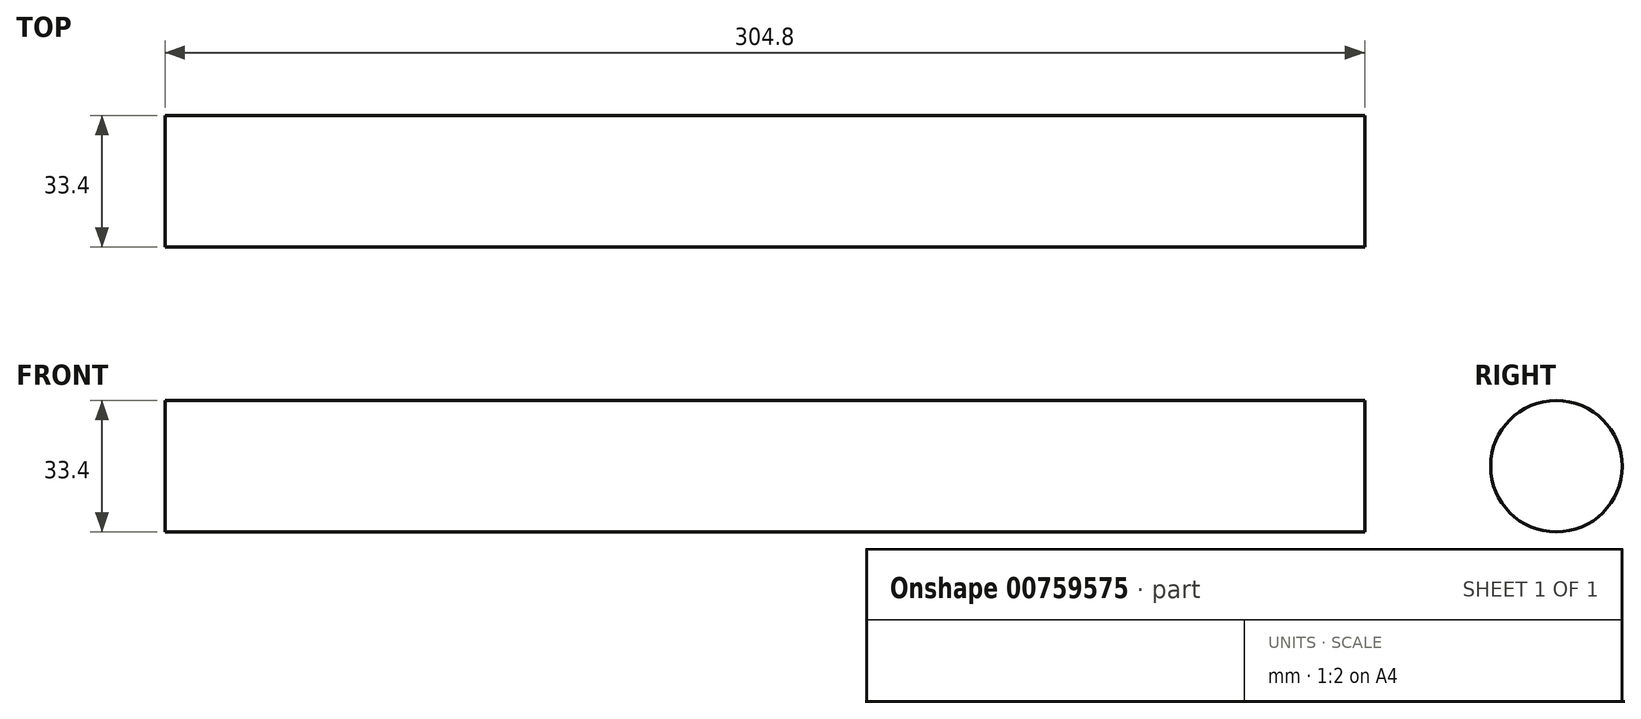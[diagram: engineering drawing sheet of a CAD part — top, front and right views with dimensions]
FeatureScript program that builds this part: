
annotation { "Feature Type Name" : "Feature", "Feature Type Description" : "" }
export const myFeature = defineFeature(function(context is Context, id is Id, definition is map)
    precondition{}
    {
        {
            var Q0;
            Q0=qCreatedBy(makeId("Right.planeOp"),FACE);
            var sketch = newSketch(context, id + "F0", { "sketchPlane" : qUnion([Q0])});
            skCircle(sketch, "E0", {"center": v(0, -1.48) * mm, "radius": 16.7 * mm});
            skSolve(sketch);
        }
        {
            var Q0;
            Q0 = qSketchRegion(id + "F0", true);
            extrude(context, id + "F1", {"entities" : qUnion([Q0]), "endBound" : BoundingType.SYMMETRIC, "depth" : 304.8 * mm, "offsetDistance" : 25.4 * mm});
        }
    });
